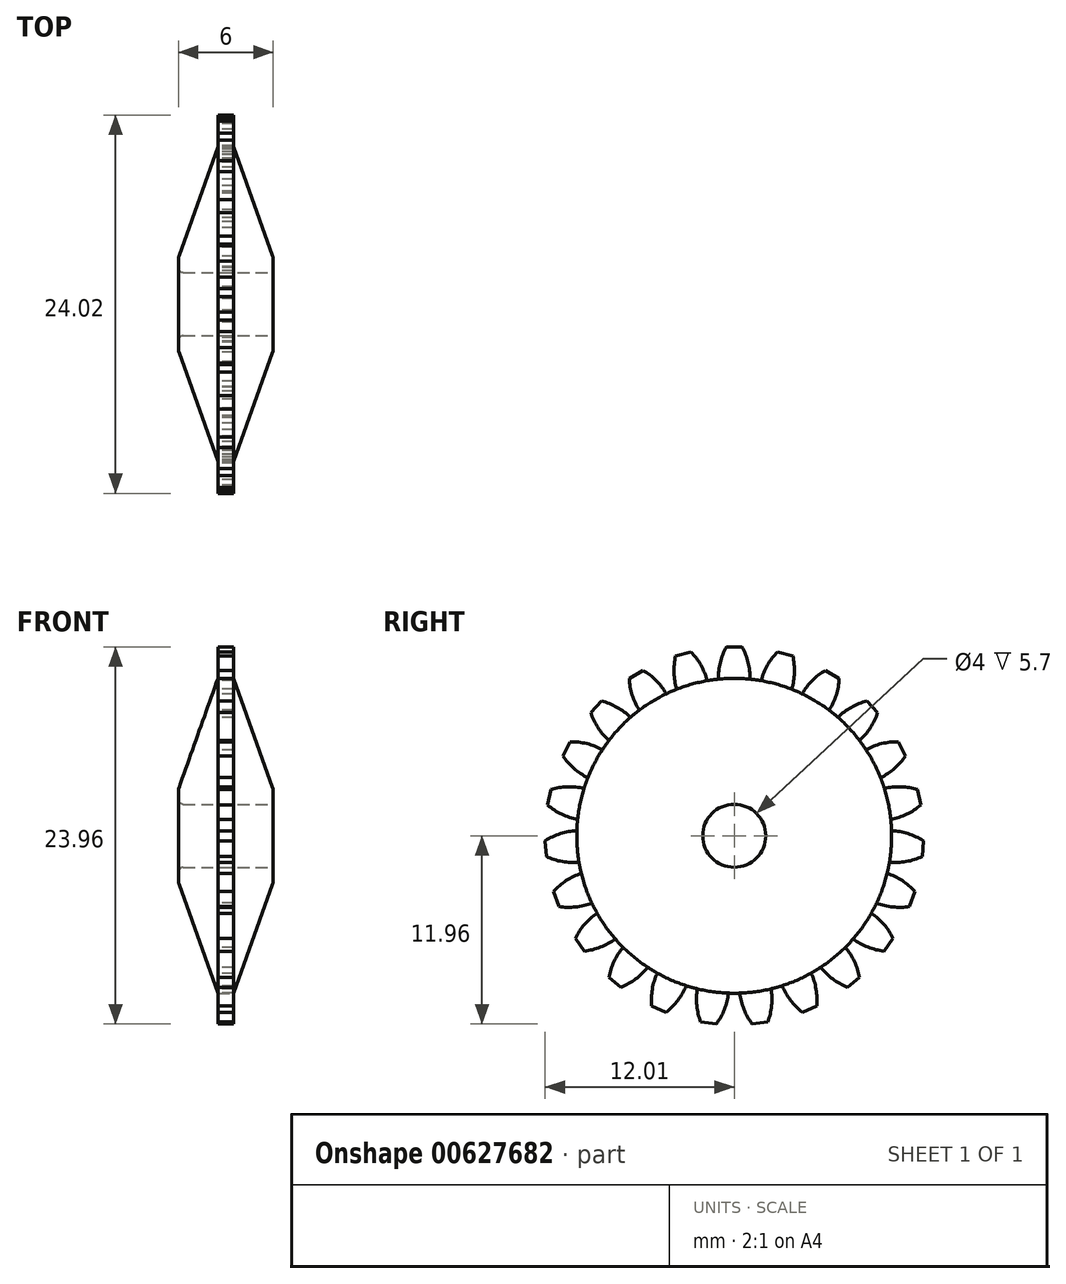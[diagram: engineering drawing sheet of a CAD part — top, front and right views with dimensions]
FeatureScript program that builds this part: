
annotation { "Feature Type Name" : "Feature", "Feature Type Description" : "" }
export const myFeature = defineFeature(function(context is Context, id is Id, definition is map)
    precondition{}
    {
        {
            var Q0;
            Q0=qCreatedBy(makeId("Front.planeOp"),FACE);
            var sketch = newSketch(context, id + "F0", { "sketchPlane" : qUnion([Q0])});
            skLineSegment(sketch, "E0", {"start": v(0, 0) * mm, "end": v(0, 10) * mm});
            skLineSegment(sketch, "E1", {"start": v(0, 10) * mm, "end": v(0.5, 10) * mm});
            skLineSegment(sketch, "E2", {"start": v(0.5, 10) * mm, "end": v(3, 3) * mm});
            skLineSegment(sketch, "E3", {"start": v(3, 3) * mm, "end": v(3, 0) * mm});
            skLineSegment(sketch, "E4", {"start": v(3, 0) * mm, "end": v(0, 0) * mm});
            skSolve(sketch);
        }
        {
            var Q0;
            Q0 = qSketchRegion(id + "F0", true);
            var Q1;
            Q1=sQuery(id+"F0.wireOp",EDGE,"E4");
            revolve(context, id + "F1", {"entities" : qUnion([Q0]), "axis" : qUnion([Q1]), "revolveType" : RevolveType.FULL});
        }
        {
            var Q0;
            Q0=makeQuery(id+"F1.opRevolve","SWEPT_BODY",BODY,{"disambiguationData":[OSD([sQuery(id+"F0.wireOp",EDGE,"E0"),sQuery(id+"F0.wireOp",EDGE,"E1"),sQuery(id+"F0.wireOp",EDGE,"E2"),sQuery(id+"F0.wireOp",EDGE,"E3"),sQuery(id+"F0.wireOp",EDGE,"E4")])]});
            var Q1;
            Q1=qCreatedBy(makeId("Right.planeOp"),FACE);
            mirror(context, id + "F2", {"operationType" : NewBodyOperationType.ADD, "entities" : qUnion([Q0]), "mirrorPlane" : qUnion([Q1])});
        }
        {
            var Q0;
            Q0=makeQuery(id+"F1.opRevolve","SWEPT_FACE",FACE,{"disambiguationData":[OSD([sQuery(id+"F0.wireOp",EDGE,"E3")])]});
            var sketch = newSketch(context, id + "F3", { "sketchPlane" : qUnion([Q0])});
            skCircle(sketch, "E5", {"center": v(0, 0) * mm, "radius": 2 * mm});
            skSolve(sketch);
        }
        {
            var Q0;
            Q0 = qSketchRegion(id + "F3", true);
            extrude(context, id + "F4", {"entities" : qUnion([Q0]), "operationType" : NewBodyOperationType.REMOVE, "endBound" : BoundingType.THROUGH_ALL, "oppositeDirection" : true, "depth" : 25 * mm, "offsetDistance" : 25 * mm});
        }
        {
            var Q0;
            Q0=qCreatedBy(makeId("Right.planeOp"),FACE);
            var sketch = newSketch(context, id + "F5", { "sketchPlane" : qUnion([Q0])});
            skLineSegment(sketch, "E6", {"start": v(0, 6.86) * mm, "end": v(0, 12) * mm, "construction": true});
            skLineSegment(sketch, "E7", {"start": v(0.5, 12) * mm, "end": v(-0.5, 12) * mm});
            skCircle(sketch, "E8.0", {"center": v(0, 0) * mm, "radius": 10 * mm});
            skArc(sketch, "E9", {"start": v(-0.5, 12) * mm, "mid": v(-0.89, 11) * mm, "end": v(-1, 9.95) * mm});
            skArc(sketch, "E10", {"start": v(1, 9.95) * mm, "mid": v(0.89, 11) * mm, "end": v(0.5, 12) * mm});
            skArc(sketch, "E11.1.0", {"start": v(-3.72, 11.42) * mm, "mid": v(-3.82, 10.36) * mm, "end": v(-3.65, 9.31) * mm});
            skLineSegment(sketch, "E11.1.1", {"start": v(-2.76, 11.69) * mm, "end": v(-3.72, 11.42) * mm});
            skArc(sketch, "E11.1.2", {"start": v(-1.72, 9.85) * mm, "mid": v(-2.12, 10.84) * mm, "end": v(-2.76, 11.69) * mm});
            skArc(sketch, "E11.2.0", {"start": v(-6.66, 10) * mm, "mid": v(-6.48, 8.94) * mm, "end": v(-6.02, 7.98) * mm});
            skLineSegment(sketch, "E11.2.1", {"start": v(-5.8, 10.51) * mm, "end": v(-6.66, 10) * mm});
            skArc(sketch, "E11.2.2", {"start": v(-4.32, 9.02) * mm, "mid": v(-4.96, 9.87) * mm, "end": v(-5.8, 10.51) * mm});
            skArc(sketch, "E11.3.0", {"start": v(-9.11, 7.83) * mm, "mid": v(-8.65, 6.87) * mm, "end": v(-7.95, 6.06) * mm});
            skLineSegment(sketch, "E11.3.1", {"start": v(-8.43, 8.56) * mm, "end": v(-9.11, 7.83) * mm});
            skArc(sketch, "E11.3.2", {"start": v(-6.59, 7.52) * mm, "mid": v(-7.44, 8.16) * mm, "end": v(-8.43, 8.56) * mm});
            skArc(sketch, "E11.4.0", {"start": v(-10.88, 5.08) * mm, "mid": v(-10.18, 4.28) * mm, "end": v(-9.3, 3.69) * mm});
            skLineSegment(sketch, "E11.4.1", {"start": v(-10.42, 5.96) * mm, "end": v(-10.88, 5.08) * mm});
            skArc(sketch, "E11.4.2", {"start": v(-8.37, 5.47) * mm, "mid": v(-9.37, 5.85) * mm, "end": v(-10.42, 5.96) * mm});
            skArc(sketch, "E11.5.0", {"start": v(-11.85, 1.95) * mm, "mid": v(-10.96, 1.37) * mm, "end": v(-9.95, 1.05) * mm});
            skLineSegment(sketch, "E11.5.1", {"start": v(-11.65, 2.93) * mm, "end": v(-11.85, 1.95) * mm});
            skArc(sketch, "E11.5.2", {"start": v(-9.54, 3) * mm, "mid": v(-10.6, 3.1) * mm, "end": v(-11.65, 2.93) * mm});
            skArc(sketch, "E11.6.0", {"start": v(-11.94, -1.32) * mm, "mid": v(-10.92, -1.64) * mm, "end": v(-9.86, -1.68) * mm});
            skLineSegment(sketch, "E11.6.1", {"start": v(-12, -0.32) * mm, "end": v(-11.94, -1.32) * mm});
            skArc(sketch, "E11.6.2", {"start": v(-10, 0.32) * mm, "mid": v(-11.04, 0.13) * mm, "end": v(-12, -0.32) * mm});
            skArc(sketch, "E11.7.0", {"start": v(-11.14, -4.49) * mm, "mid": v(-10.08, -4.52) * mm, "end": v(-9.04, -4.27) * mm});
            skLineSegment(sketch, "E11.7.1", {"start": v(-11.47, -3.55) * mm, "end": v(-11.14, -4.49) * mm});
            skArc(sketch, "E11.7.2", {"start": v(-9.71, -2.39) * mm, "mid": v(-10.67, -2.85) * mm, "end": v(-11.47, -3.55) * mm});
            skArc(sketch, "E11.8.0", {"start": v(-9.52, -7.33) * mm, "mid": v(-8.48, -7.07) * mm, "end": v(-7.55, -6.55) * mm});
            skLineSegment(sketch, "E11.8.1", {"start": v(-10.1, -6.51) * mm, "end": v(-9.52, -7.33) * mm});
            skArc(sketch, "E11.8.2", {"start": v(-8.7, -4.92) * mm, "mid": v(-9.5, -5.62) * mm, "end": v(-10.1, -6.51) * mm});
            skArc(sketch, "E11.9.0", {"start": v(-7.19, -9.62) * mm, "mid": v(-6.26, -9.1) * mm, "end": v(-5.5, -8.35) * mm});
            skLineSegment(sketch, "E11.9.1", {"start": v(-7.96, -9) * mm, "end": v(-7.19, -9.62) * mm});
            skArc(sketch, "E11.9.2", {"start": v(-7.05, -7.09) * mm, "mid": v(-7.64, -7.98) * mm, "end": v(-7.96, -9) * mm});
            skArc(sketch, "E11.10.0", {"start": v(-4.32, -11.2) * mm, "mid": v(-3.57, -10.45) * mm, "end": v(-3.05, -9.52) * mm});
            skLineSegment(sketch, "E11.10.1", {"start": v(-5.24, -10.8) * mm, "end": v(-4.32, -11.2) * mm});
            skArc(sketch, "E11.10.2", {"start": v(-4.88, -8.73) * mm, "mid": v(-5.2, -9.74) * mm, "end": v(-5.24, -10.8) * mm});
            skArc(sketch, "E11.11.0", {"start": v(-1.14, -11.96) * mm, "mid": v(-0.62, -11.03) * mm, "end": v(-0.36, -10) * mm});
            skLineSegment(sketch, "E11.11.1", {"start": v(-2.13, -11.82) * mm, "end": v(-1.14, -11.96) * mm});
            skArc(sketch, "E11.11.2", {"start": v(-2.35, -9.72) * mm, "mid": v(-2.38, -10.79) * mm, "end": v(-2.13, -11.82) * mm});
            skArc(sketch, "E11.12.0", {"start": v(2.13, -11.82) * mm, "mid": v(2.38, -10.79) * mm, "end": v(2.35, -9.72) * mm});
            skLineSegment(sketch, "E11.12.1", {"start": v(1.14, -11.96) * mm, "end": v(2.13, -11.82) * mm});
            skArc(sketch, "E11.12.2", {"start": v(0.36, -10) * mm, "mid": v(0.62, -11.03) * mm, "end": v(1.14, -11.96) * mm});
            skArc(sketch, "E11.13.0", {"start": v(5.24, -10.8) * mm, "mid": v(5.2, -9.74) * mm, "end": v(4.88, -8.73) * mm});
            skLineSegment(sketch, "E11.13.1", {"start": v(4.32, -11.2) * mm, "end": v(5.24, -10.8) * mm});
            skArc(sketch, "E11.13.2", {"start": v(3.05, -9.52) * mm, "mid": v(3.57, -10.45) * mm, "end": v(4.32, -11.2) * mm});
            skArc(sketch, "E11.14.0", {"start": v(7.96, -9) * mm, "mid": v(7.64, -7.98) * mm, "end": v(7.05, -7.09) * mm});
            skLineSegment(sketch, "E11.14.1", {"start": v(7.19, -9.62) * mm, "end": v(7.96, -9) * mm});
            skArc(sketch, "E11.14.2", {"start": v(5.5, -8.35) * mm, "mid": v(6.26, -9.1) * mm, "end": v(7.19, -9.62) * mm});
            skArc(sketch, "E11.15.0", {"start": v(10.1, -6.51) * mm, "mid": v(9.5, -5.62) * mm, "end": v(8.7, -4.92) * mm});
            skLineSegment(sketch, "E11.15.1", {"start": v(9.52, -7.33) * mm, "end": v(10.1, -6.51) * mm});
            skArc(sketch, "E11.15.2", {"start": v(7.55, -6.55) * mm, "mid": v(8.48, -7.07) * mm, "end": v(9.52, -7.33) * mm});
            skArc(sketch, "E11.16.0", {"start": v(11.47, -3.55) * mm, "mid": v(10.67, -2.85) * mm, "end": v(9.71, -2.39) * mm});
            skLineSegment(sketch, "E11.16.1", {"start": v(11.14, -4.49) * mm, "end": v(11.47, -3.55) * mm});
            skArc(sketch, "E11.16.2", {"start": v(9.04, -4.27) * mm, "mid": v(10.08, -4.52) * mm, "end": v(11.14, -4.49) * mm});
            skArc(sketch, "E11.17.0", {"start": v(12, -0.32) * mm, "mid": v(11.04, 0.13) * mm, "end": v(10, 0.32) * mm});
            skLineSegment(sketch, "E11.17.1", {"start": v(11.94, -1.32) * mm, "end": v(12, -0.32) * mm});
            skArc(sketch, "E11.17.2", {"start": v(9.86, -1.68) * mm, "mid": v(10.92, -1.64) * mm, "end": v(11.94, -1.32) * mm});
            skArc(sketch, "E11.18.0", {"start": v(11.65, 2.93) * mm, "mid": v(10.6, 3.1) * mm, "end": v(9.54, 3) * mm});
            skLineSegment(sketch, "E11.18.1", {"start": v(11.85, 1.95) * mm, "end": v(11.65, 2.93) * mm});
            skArc(sketch, "E11.18.2", {"start": v(9.95, 1.05) * mm, "mid": v(10.96, 1.37) * mm, "end": v(11.85, 1.95) * mm});
            skArc(sketch, "E11.19.0", {"start": v(10.42, 5.96) * mm, "mid": v(9.37, 5.85) * mm, "end": v(8.37, 5.47) * mm});
            skLineSegment(sketch, "E11.19.1", {"start": v(10.88, 5.08) * mm, "end": v(10.42, 5.96) * mm});
            skArc(sketch, "E11.19.2", {"start": v(9.3, 3.69) * mm, "mid": v(10.18, 4.28) * mm, "end": v(10.88, 5.08) * mm});
            skArc(sketch, "E11.20.0", {"start": v(8.43, 8.56) * mm, "mid": v(7.44, 8.16) * mm, "end": v(6.59, 7.52) * mm});
            skLineSegment(sketch, "E11.20.1", {"start": v(9.11, 7.83) * mm, "end": v(8.43, 8.56) * mm});
            skArc(sketch, "E11.20.2", {"start": v(7.95, 6.06) * mm, "mid": v(8.65, 6.87) * mm, "end": v(9.11, 7.83) * mm});
            skArc(sketch, "E11.21.0", {"start": v(5.8, 10.51) * mm, "mid": v(4.96, 9.87) * mm, "end": v(4.32, 9.02) * mm});
            skLineSegment(sketch, "E11.21.1", {"start": v(6.66, 10) * mm, "end": v(5.8, 10.51) * mm});
            skArc(sketch, "E11.21.2", {"start": v(6.02, 7.98) * mm, "mid": v(6.48, 8.94) * mm, "end": v(6.66, 10) * mm});
            skArc(sketch, "E11.22.0", {"start": v(2.76, 11.69) * mm, "mid": v(2.12, 10.84) * mm, "end": v(1.72, 9.85) * mm});
            skLineSegment(sketch, "E11.22.1", {"start": v(3.72, 11.42) * mm, "end": v(2.76, 11.69) * mm});
            skArc(sketch, "E11.22.2", {"start": v(3.65, 9.31) * mm, "mid": v(3.82, 10.36) * mm, "end": v(3.72, 11.42) * mm});
            skSolve(sketch);
        }
        {
            var Q0;
            Q0=makeQuery(id+"F5.imprint","IMPRINT",FACE,{"disambiguationData":[TD([[makeQuery(id+"F5.imprint","IMPRINT",EDGE,{"derivedFrom":sQuery(id+"F5.wireOp",EDGE,"E7")}),1.0]])]});
            var Q1;
            {var subQ0=sQuery(id+"F5.wireOp",EDGE,"E11.1.0");Q1=makeQuery(id+"F5.imprint","IMPRINT",FACE,{"disambiguationData":[TD([[makeQuery(id+"F5.imprint","IMPRINT",EDGE,{"derivedFrom":subQ0}),1.0]])]});}
            var Q2;
            {var subQ0=sQuery(id+"F5.wireOp",EDGE,"E11.2.0");Q2=makeQuery(id+"F5.imprint","IMPRINT",FACE,{"disambiguationData":[TD([[makeQuery(id+"F5.imprint","IMPRINT",EDGE,{"derivedFrom":subQ0}),1.0]])]});}
            var Q3;
            {var subQ0=sQuery(id+"F5.wireOp",EDGE,"E11.3.0");Q3=makeQuery(id+"F5.imprint","IMPRINT",FACE,{"disambiguationData":[TD([[makeQuery(id+"F5.imprint","IMPRINT",EDGE,{"derivedFrom":subQ0}),1.0]])]});}
            var Q4;
            {var subQ0=sQuery(id+"F5.wireOp",EDGE,"E11.4.0");Q4=makeQuery(id+"F5.imprint","IMPRINT",FACE,{"disambiguationData":[TD([[makeQuery(id+"F5.imprint","IMPRINT",EDGE,{"derivedFrom":subQ0}),1.0]])]});}
            var Q5;
            {var subQ0=sQuery(id+"F5.wireOp",EDGE,"E11.5.0");Q5=makeQuery(id+"F5.imprint","IMPRINT",FACE,{"disambiguationData":[TD([[makeQuery(id+"F5.imprint","IMPRINT",EDGE,{"derivedFrom":subQ0}),1.0]])]});}
            var Q6;
            {var subQ0=sQuery(id+"F5.wireOp",EDGE,"E11.6.0");Q6=makeQuery(id+"F5.imprint","IMPRINT",FACE,{"disambiguationData":[TD([[makeQuery(id+"F5.imprint","IMPRINT",EDGE,{"derivedFrom":subQ0}),1.0]])]});}
            var Q7;
            {var subQ0=sQuery(id+"F5.wireOp",EDGE,"E11.7.0");Q7=makeQuery(id+"F5.imprint","IMPRINT",FACE,{"disambiguationData":[TD([[makeQuery(id+"F5.imprint","IMPRINT",EDGE,{"derivedFrom":subQ0}),1.0]])]});}
            var Q8;
            {var subQ0=sQuery(id+"F5.wireOp",EDGE,"E11.8.0");Q8=makeQuery(id+"F5.imprint","IMPRINT",FACE,{"disambiguationData":[TD([[makeQuery(id+"F5.imprint","IMPRINT",EDGE,{"derivedFrom":subQ0}),1.0]])]});}
            var Q9;
            {var subQ0=sQuery(id+"F5.wireOp",EDGE,"E11.9.0");Q9=makeQuery(id+"F5.imprint","IMPRINT",FACE,{"disambiguationData":[TD([[makeQuery(id+"F5.imprint","IMPRINT",EDGE,{"derivedFrom":subQ0}),1.0]])]});}
            var Q10;
            {var subQ0=sQuery(id+"F5.wireOp",EDGE,"E11.10.0");Q10=makeQuery(id+"F5.imprint","IMPRINT",FACE,{"disambiguationData":[TD([[makeQuery(id+"F5.imprint","IMPRINT",EDGE,{"derivedFrom":subQ0}),1.0]])]});}
            var Q11;
            {var subQ0=sQuery(id+"F5.wireOp",EDGE,"E11.11.0");Q11=makeQuery(id+"F5.imprint","IMPRINT",FACE,{"disambiguationData":[TD([[makeQuery(id+"F5.imprint","IMPRINT",EDGE,{"derivedFrom":subQ0}),1.0]])]});}
            var Q12;
            {var subQ0=sQuery(id+"F5.wireOp",EDGE,"E11.12.0");Q12=makeQuery(id+"F5.imprint","IMPRINT",FACE,{"disambiguationData":[TD([[makeQuery(id+"F5.imprint","IMPRINT",EDGE,{"derivedFrom":subQ0}),1.0]])]});}
            var Q13;
            {var subQ0=sQuery(id+"F5.wireOp",EDGE,"E11.13.0");Q13=makeQuery(id+"F5.imprint","IMPRINT",FACE,{"disambiguationData":[TD([[makeQuery(id+"F5.imprint","IMPRINT",EDGE,{"derivedFrom":subQ0}),1.0]])]});}
            var Q14;
            {var subQ0=sQuery(id+"F5.wireOp",EDGE,"E11.14.0");Q14=makeQuery(id+"F5.imprint","IMPRINT",FACE,{"disambiguationData":[TD([[makeQuery(id+"F5.imprint","IMPRINT",EDGE,{"derivedFrom":subQ0}),1.0]])]});}
            var Q15;
            {var subQ0=sQuery(id+"F5.wireOp",EDGE,"E11.15.0");Q15=makeQuery(id+"F5.imprint","IMPRINT",FACE,{"disambiguationData":[TD([[makeQuery(id+"F5.imprint","IMPRINT",EDGE,{"derivedFrom":subQ0}),1.0]])]});}
            var Q16;
            {var subQ0=sQuery(id+"F5.wireOp",EDGE,"E11.16.0");Q16=makeQuery(id+"F5.imprint","IMPRINT",FACE,{"disambiguationData":[TD([[makeQuery(id+"F5.imprint","IMPRINT",EDGE,{"derivedFrom":subQ0}),1.0]])]});}
            var Q17;
            {var subQ0=sQuery(id+"F5.wireOp",EDGE,"E11.17.0");Q17=makeQuery(id+"F5.imprint","IMPRINT",FACE,{"disambiguationData":[TD([[makeQuery(id+"F5.imprint","IMPRINT",EDGE,{"derivedFrom":subQ0}),1.0]])]});}
            var Q18;
            {var subQ0=sQuery(id+"F5.wireOp",EDGE,"E11.18.0");Q18=makeQuery(id+"F5.imprint","IMPRINT",FACE,{"disambiguationData":[TD([[makeQuery(id+"F5.imprint","IMPRINT",EDGE,{"derivedFrom":subQ0}),1.0]])]});}
            var Q19;
            {var subQ0=sQuery(id+"F5.wireOp",EDGE,"E11.19.0");Q19=makeQuery(id+"F5.imprint","IMPRINT",FACE,{"disambiguationData":[TD([[makeQuery(id+"F5.imprint","IMPRINT",EDGE,{"derivedFrom":subQ0}),1.0]])]});}
            var Q20;
            {var subQ0=sQuery(id+"F5.wireOp",EDGE,"E11.20.0");Q20=makeQuery(id+"F5.imprint","IMPRINT",FACE,{"disambiguationData":[TD([[makeQuery(id+"F5.imprint","IMPRINT",EDGE,{"derivedFrom":subQ0}),1.0]])]});}
            var Q21;
            {var subQ0=sQuery(id+"F5.wireOp",EDGE,"E11.21.0");Q21=makeQuery(id+"F5.imprint","IMPRINT",FACE,{"disambiguationData":[TD([[makeQuery(id+"F5.imprint","IMPRINT",EDGE,{"derivedFrom":subQ0}),1.0]])]});}
            var Q22;
            {var subQ0=sQuery(id+"F5.wireOp",EDGE,"E11.22.0");Q22=makeQuery(id+"F5.imprint","IMPRINT",FACE,{"disambiguationData":[TD([[makeQuery(id+"F5.imprint","IMPRINT",EDGE,{"derivedFrom":subQ0}),1.0]])]});}
            extrude(context, id + "F6", {"entities" : qUnion([Q0, Q1, Q2, Q3, Q4, Q5, Q6, Q7, Q8, Q9, Q10, Q11, Q12, Q13, Q14, Q15, Q16, Q17, Q18, Q19, Q20, Q21, Q22]), "operationType" : NewBodyOperationType.ADD, "endBound" : BoundingType.SYMMETRIC, "depth" : 1 * mm, "offsetDistance" : 25 * mm});
        }
        {
            var Q0;
            Q0=makeQuery(id+"F4.boolean.opBoolean","COPY",EDGE,{"derivedFrom":makeQuery(id+"F4.opExtrude","CAP_EDGE",EDGE,{"disambiguationData":[OSD([sQuery(id+"F3.wireOp",EDGE,"E5")])],"isStart":true})});
            var Q1;
            Q1=makeQuery(id+"F4.boolean.opBoolean","INTERSECT",EDGE,{"derivedFrom":[makeQuery(id+"F2.opPattern","COPY",FACE,{"derivedFrom":makeQuery(id+"F1.opRevolve","SWEPT_FACE",FACE,{"disambiguationData":[OSD([sQuery(id+"F0.wireOp",EDGE,"E3")])]}),"instanceName":"1"}),makeQuery(id+"F4.opExtrude","SWEPT_FACE",FACE,{"disambiguationData":[OSD([sQuery(id+"F3.wireOp",EDGE,"E5")])]})]});
            var Q2;
            Q2=makeQuery(id+"F2.opPattern","COPY",EDGE,{"derivedFrom":makeQuery(id+"F1.opRevolve","SWEPT_EDGE",EDGE,{"disambiguationData":[OSD([sQuery(id+"F0.wireOp",EDGE,"E2"),sQuery(id+"F0.wireOp",EDGE,"E3")])]}),"instanceName":"1"});
            var Q3;
            Q3=makeQuery(id+"F1.opRevolve","SWEPT_EDGE",EDGE,{"disambiguationData":[OSD([sQuery(id+"F0.wireOp",EDGE,"E2"),sQuery(id+"F0.wireOp",EDGE,"E3")])]});
            fillet(context, id + "F7", {"entities" : qUnion([Q0, Q1, Q2, Q3]), "radius" : 0.3 * mm, "tangentPropagation" : true, "allowEdgeOverflow" : false});
        }
    });
